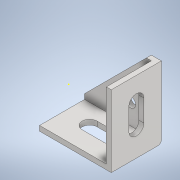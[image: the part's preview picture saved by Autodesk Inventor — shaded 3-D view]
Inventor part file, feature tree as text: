
AUTODESK INVENTOR PART (.ipt)
format: ipt  version: 2021 (Build 250183000, 183)  size: 124,416 bytes
history: native  units: in
note: dims shown in document units (in); Inventor stores cm internally (conversion verified against a paired STEP export)
features: other x2, sketch x2
ambient origin geometry x8: Origin, YZ Plane, XZ Plane, XY Plane, X Axis, Y Axis, Z Axis, Center Point
bodies: Body1 (feature_tree)
feature tree (4):
  other  "Sólido2"
  sketch  "Boceto1"
  sketch  "Boceto2"
  other  "Sólido1"
